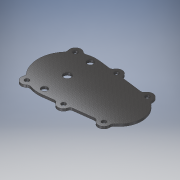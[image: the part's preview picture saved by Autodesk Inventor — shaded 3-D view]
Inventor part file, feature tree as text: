
AUTODESK INVENTOR PART (.ipt)
format: ipt  version: 2017 (Build 210142000, 142)  size: 223,232 bytes
history: native  units: mm
features: extrude x3, sketch x3, other x1, fillet x1
ambient origin geometry x8: Origin, YZ Plane, XZ Plane, XY Plane, X Axis, Y Axis, Z Axis, Center Point
bodies: Body1 (feature_tree)
feature tree (8):
  other  "Sólido1"
  extrude  "Extrusión1"  Depth=88.9mm
  extrude  "Extrusión2"  Depth=22.225mm
  fillet  "Empalme1"  Radius=22.225mm
  extrude  "Extrusión3"  Depth=45.0mm
  sketch  "Boceto1"  dims[d0=114.3mm d1=88.9mm]
  sketch  "Boceto2"  dims[d2=203.2mm d3=22.225mm d4=22.225mm]
  sketch  "Boceto3"  dims[d7=22.225mm d8=22.225mm d11=22.225mm d13=0.0mm d14=22.225mm d16=4.445mm d17=0.0mm d18=8.4328mm d19=8.4328mm d20=8.4328mm d21=8.4328mm d22=8.4328mm d23=8.4328mm d24=25.4mm d25=0.0mm d26=6.35mm d27=12.7mm d28=12.7mm d29=44.45mm d30=44.45mm d31=31.75mm d32=31.75mm d33=14.2875mm d34=12.0mm d35=12.0mm d36=45.0mm d37=45.0mm d38=25.4mm d39=0.0mm]
